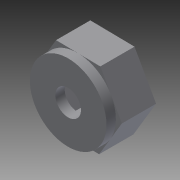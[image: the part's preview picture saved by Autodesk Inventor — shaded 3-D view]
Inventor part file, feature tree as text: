
AUTODESK INVENTOR PART (.ipt)
format: ipt  version: 2014 (Build 180170000, 170)  size: 109,568 bytes
history: native  units: in
note: dims shown in document units (in); Inventor stores cm internally (conversion verified against a paired STEP export)
features: reference x6, extrude x2, sketch x2
ambient origin geometry x8: Origin, YZ Plane, XZ Plane, XY Plane, X Axis, Y Axis, Z Axis, Center Point
bodies: Solid1 (feature_tree)
feature tree (10):
  extrude  "Extrusion1"  Depth=0.315in TaperAngle=0.0deg
  extrude  "Extrusion2"  Depth=0.0866in TaperAngle=0.0deg
  sketch  "Sketch2"  dims[d0=0.1181in d1=0.315in d2=0.0in]
  reference  "Reference1"
  reference  "Reference2"
  reference  "Reference3"
  reference  "Reference4"
  reference  "Reference5"
  reference  "Reference6"
  sketch  "Sketch3"  dims[d3=0.2362in d4=0.0866in d5=0.0in]
